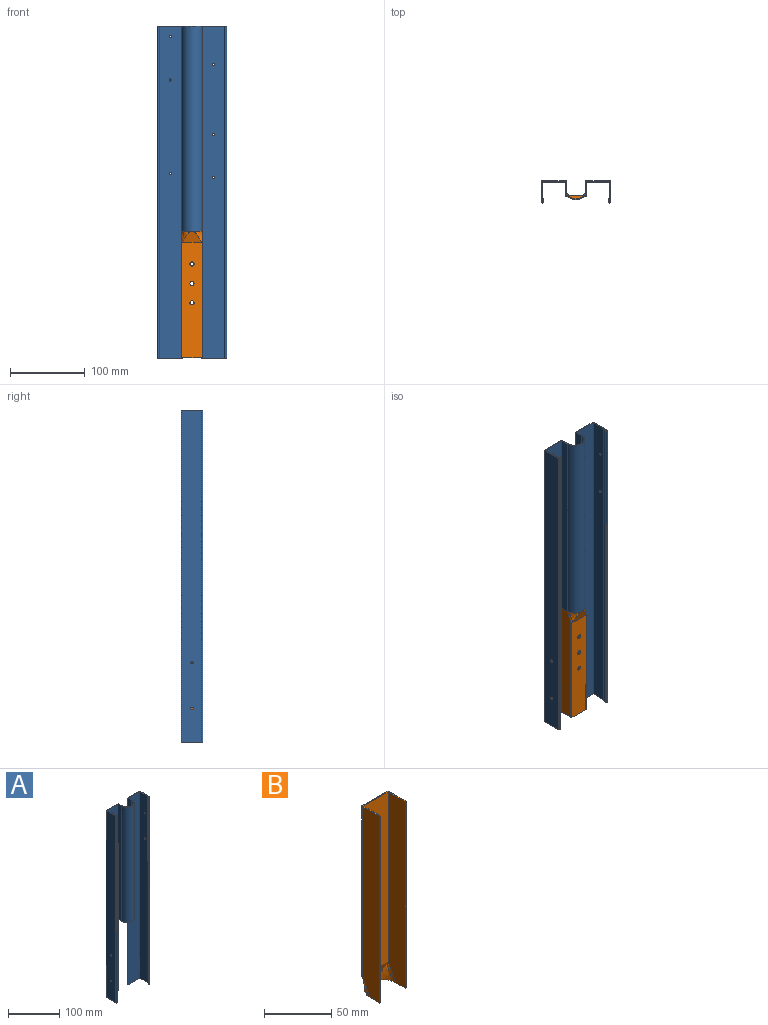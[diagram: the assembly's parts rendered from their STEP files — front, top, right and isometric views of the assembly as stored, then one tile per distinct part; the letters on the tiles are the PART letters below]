
ASSEMBLY  parts=2 mates=1
PART A: 38 faces, bbox 93x29x445 mm
  f0: cylinder r=13mm len=275mm, axis (0,0,-1), area 11231.2mm2, adj f6,f7,f8,f37
  f1: plane 275x10mm, normal (-1,0,0), area 2750mm2, adj f2,f6,f17,f37
  f2: cylinder r=14mm len=275mm, axis (0,0,-1), area 12095.1mm2, adj f1,f3,f6,f37
  f3: plane 275x10mm, normal (1,0,0), area 2750mm2, adj f2,f6,f18,f37
  f4: plane 33.5x29mm, normal (0,0,-1), area 68.6mm2, adj f8,f9,f10,f11,f12,f13,f14,f15
  f5: plane 33.5x29mm, normal (0,0,-1), area 68.6mm2, adj f7,f18,f19,f20,f21,f22,f23,f24
  f6: plane 93x29mm, normal (0,0,1), area 199.7mm2, adj f0,f1,f2,f3,f7,f8,f9,f10
  f7: plane 445x11mm, normal (-1,0,0), area 3195mm2, adj f0,f5,f6,f18,f25,f37
  f8: plane 445x11mm, normal (1,0,0), area 3195mm2, adj f0,f4,f6,f9,f17,f37
  f9: plane 445x33.5mm, normal (0,1,0), area 14886.3mm2, adj f4,f6,f8,f10,f28,f29,f36
  f10: plane 445x27.5mm, normal (-1,0,0), area 12223.4mm2, adj f4,f6,f9,f11,f32,f33
  f11: cylinder r=1.5mm len=445mm, axis (0,0,-1), area 2209.5mm2, adj f4,f6,f10,f12
  f12: plane 445x5.25mm, normal (0.99,0.17,0), area 2369.1mm2, adj f4,f6,f11,f13
  f13: plane 445x0.99mm, normal (-0.17,0.99,0), area 445mm2, adj f4,f6,f12,f14
  f14: plane 445x5.25mm, normal (-0.99,-0.17,0), area 2369.1mm2, adj f4,f6,f13,f15
  f15: cylinder r=0.5mm len=445mm, axis (0,0,-1), area 736.5mm2, adj f4,f6,f14,f16
  f16: plane 445x26.5mm, normal (1,0,0), area 11778.4mm2, adj f4,f6,f15,f17,f32,f33
  f17: plane 445x32.5mm, normal (0,-1,0), area 14166.3mm2, adj f1,f4,f6,f8,f16,f28,f29,f36
  f18: plane 445x32.5mm, normal (0,-1,0), area 14166.3mm2, adj f3,f5,f6,f7,f19,f27,f34,f35
  f19: plane 445x26.5mm, normal (-1,0,0), area 11778.4mm2, adj f5,f6,f18,f20,f30,f31
  f20: cylinder r=0.5mm len=445mm, axis (0,0,-1), area 736.5mm2, adj f5,f6,f19,f21
  f21: plane 445x5.25mm, normal (0.99,-0.17,0), area 2369.1mm2, adj f5,f6,f20,f22
  f22: plane 445x0.99mm, normal (0.17,0.99,0), area 445mm2, adj f5,f6,f21,f23
  f23: plane 445x5.25mm, normal (-0.99,0.17,0), area 2369.1mm2, adj f5,f6,f22,f24
  f24: cylinder r=1.5mm len=445mm, axis (0,0,-1), area 2209.5mm2, adj f5,f6,f23,f26
  f25: plane 445x33.5mm, normal (0,1,0), area 14886.3mm2, adj f5,f6,f7,f26,f27,f34,f35
  f26: plane 445x27.5mm, normal (1,0,0), area 12223.4mm2, adj f5,f6,f24,f25,f30,f31
  f27: cylinder r=1.5mm len=3mm, axis (0,-1,0), area 9.4mm2, adj f18,f25
  f28: cylinder r=1.5mm len=3mm, axis (0,-1,0), area 9.4mm2, adj f9,f17
  f29: cylinder r=1.5mm len=3mm, axis (0,-1,0), area 9.4mm2, adj f9,f17
  f30: cylinder r=1.5mm len=3mm, axis (-1,0,0), area 9.4mm2, adj f19,f26
  f31: cylinder r=1.5mm len=3mm, axis (-1,0,0), area 9.4mm2, adj f19,f26
  f32: cylinder r=1.5mm len=3mm, axis (-1,0,0), area 9.4mm2, adj f10,f16
  f33: cylinder r=1.5mm len=3mm, axis (-1,0,0), area 9.4mm2, adj f10,f16
  f34: cylinder r=1.5mm len=3mm, axis (0,-1,0), area 9.4mm2, adj f18,f25
  f35: cylinder r=1.5mm len=3mm, axis (0,-1,0), area 9.4mm2, adj f18,f25
  f36: cylinder r=1.5mm len=3mm, axis (0,-1,0), area 9.4mm2, adj f9,f17
  f37: plane 28x24mm, normal (0,0,-1), area 62.4mm2, adj f0,f1,f2,f3,f7,f8,f17,f18
PART B: 27 faces, bbox 35.2x31.2x177.2 mm
  f0: cylinder r=2.75mm len=5.5mm, axis (0,1,0), area 17.3mm2, adj f5,f17
  f1: cylinder r=2.75mm len=5.5mm, axis (0,1,0), area 17.3mm2, adj f5,f17
  f2: cylinder r=2.75mm len=5.5mm, axis (0,1,0), area 17.3mm2, adj f5,f17
  f3: cylinder r=2mm len=155mm, axis (0,0,1), area 76mm2, adj f5,f7,f12,f13
  f4: cylinder r=2mm len=155mm, axis (0,0,1), area 76mm2, adj f5,f10,f11,f13
  f5: plane 155.16x25.88mm, normal (0,-1,0), area 3944.4mm2, adj f0,f1,f2,f3,f4,f6,f7,f11
  f6: plane 31.84x20.86mm, normal (0,-0.95,-0.32), area 252.1mm2, adj f5,f7,f8,f9,f11,f22
  f7: bspline ~15.36x9.22mm, area 39.2mm2, adj f3,f5,f6,f8,f12,f22
  f8: bspline ~13.47x11.57mm, area 74.8mm2, adj f6,f7,f22
  f9: bspline ~13.47x11.57mm, area 74.8mm2, adj f6,f11,f22
  f10: plane 170x17.51mm, normal (1,0,0), area 2921.1mm2, adj f4,f11,f13,f22,f23
  f11: bspline ~15.36x9.22mm, area 39.2mm2, adj f4,f5,f6,f9,f10,f22
  f12: plane 170x17.51mm, normal (-1,0,0), area 2921.1mm2, adj f3,f7,f13,f14,f22
  f13: plane 28x19mm, normal (0,0,1), area 63.6mm2, adj f3,f4,f5,f10,f12,f14,f15,f16
  f14: plane 170x1mm, normal (0,-1,0), area 170mm2, adj f12,f13,f22,f26
  f15: cylinder r=3mm len=155mm, axis (0,0,1), area 240.9mm2, adj f13,f17,f19,f26
  f16: cylinder r=3mm len=155mm, axis (0,0,1), area 240.9mm2, adj f13,f17,f24,f25
  f17: plane 155x27.21mm, normal (0,1,0), area 4146.7mm2, adj f0,f1,f2,f13,f15,f16,f18
  f18: plane 34.37x22.16mm, normal (0,0.95,0.32), area 265.2mm2, adj f17,f19,f20,f21,f25
  f19: bspline ~15x9.97mm, area 49.2mm2, adj f15,f18,f20,f22,f26
  f20: bspline ~13.73x13.57mm, area 89.1mm2, adj f18,f19,f22
  f21: bspline ~13.7x13.48mm, area 89.1mm2, adj f18,f22,f25
  f22: plane 34.23x30.23mm, normal (0,0,-1), area 62.5mm2, adj f6,f7,f8,f9,f10,f11,f12,f14
  f23: plane 170x1mm, normal (0,-1,0), area 170mm2, adj f10,f13,f22,f24
  f24: plane 170x17.51mm, normal (-1,0,0), area 2921.1mm2, adj f13,f16,f22,f23,f25
  f25: bspline ~15x9.97mm, area 49.2mm2, adj f16,f18,f21,f22,f24
  f26: plane 170x17.51mm, normal (1,0,0), area 2921.1mm2, adj f13,f14,f15,f19,f22
PLACE A t=(-1.02,0.22,-791.81)mm fixed
PLACE B rot(axis=(1,0,0),180deg) t=(-1151.02,430.22,-621.81)mm
MATE fastened B.f22 <-> A.f37  axis (0,0,1) through (-1137.02,440.22,-621.81)mm
